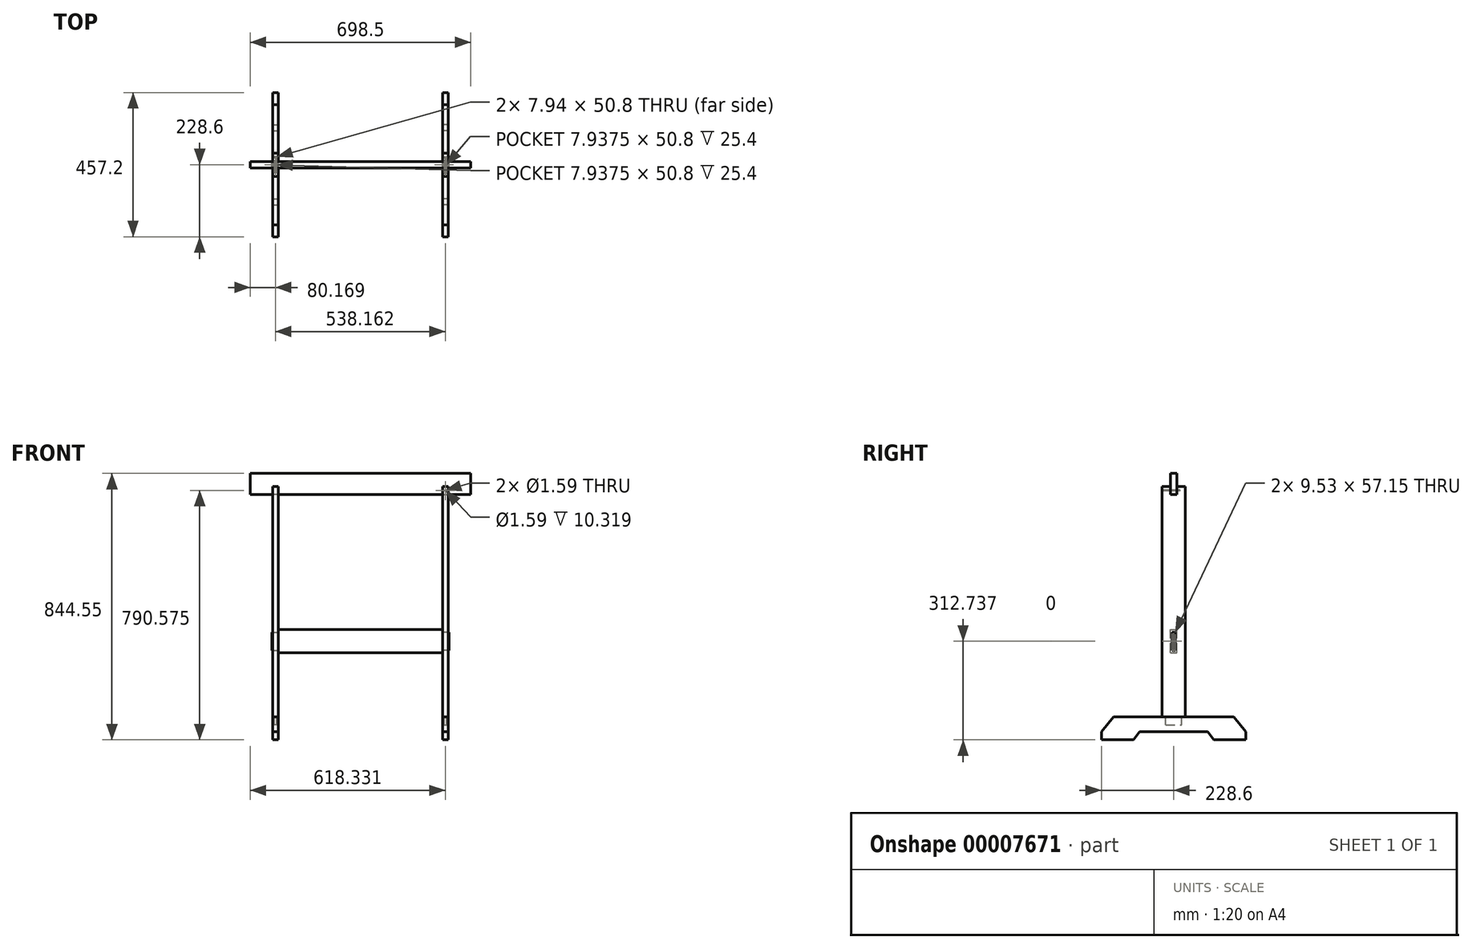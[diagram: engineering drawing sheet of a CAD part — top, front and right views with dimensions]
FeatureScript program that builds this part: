
annotation { "Feature Type Name" : "Feature", "Feature Type Description" : "" }
export const myFeature = defineFeature(function(context is Context, id is Id, definition is map)
    precondition{}
    {
        {
            var Q0;
            Q0=qCreatedBy(makeId("Right.planeOp"),FACE);
            var sketch = newSketch(context, id + "F0", { "sketchPlane" : qUnion([Q0])});
            skLineSegment(sketch, "E0.bottom", {"start": v(-36.51, 365.13) * mm, "end": v(36.51, 365.13) * mm});
            skLineSegment(sketch, "E0.top", {"start": v(-36.51, -365.13) * mm, "end": v(36.51, -365.13) * mm});
            skLineSegment(sketch, "E0.left", {"start": v(-36.51, 365.12) * mm, "end": v(-36.51, -365.13) * mm});
            skLineSegment(sketch, "E0.right", {"start": v(36.51, 365.13) * mm, "end": v(36.51, -365.13) * mm});
            skPoint(sketch, "E1", {"position": v(-36.51, 0) * mm});
            skPoint(sketch, "E2", {"position": v(0, 365.13) * mm});
            skPoint(sketch, "E3", {"position": v(0, -365.13) * mm});
            skSolve(sketch);
        }
        {
            var Q0;
            Q0=makeQuery(id+"F0.imprint","IMPRINT",FACE,{"disambiguationData":[TD([[makeQuery(id+"F0.imprint","IMPRINT",EDGE,{"derivedFrom":sQuery(id+"F0.wireOp",EDGE,"E0.bottom")}),-1.0]])]});
            extrude(context, id + "F1", {"entities" : qUnion([Q0]), "depth" : 17.46 * mm});
        }
        {
            var Q0;
            Q0=makeQuery(id+"F1.opExtrude","SWEPT_FACE",FACE,{"disambiguationData":[OSD([sQuery(id+"F0.wireOp",EDGE,"E0.top")])]});
            var sketch = newSketch(context, id + "F2", { "sketchPlane" : qUnion([Q0])});
            skLineSegment(sketch, "E4.bottom", {"start": v(4.76, 25.4) * mm, "end": v(12.7, 25.4) * mm});
            skLineSegment(sketch, "E4.top", {"start": v(4.76, -25.4) * mm, "end": v(12.7, -25.4) * mm});
            skLineSegment(sketch, "E4.left", {"start": v(4.76, 25.4) * mm, "end": v(4.76, -25.4) * mm});
            skLineSegment(sketch, "E4.right", {"start": v(12.7, 25.4) * mm, "end": v(12.7, -25.4) * mm});
            skPoint(sketch, "E5", {"position": v(4.76, 0) * mm});
            skPoint(sketch, "E6", {"position": v(8.73, 25.4) * mm});
            skLineSegment(sketch, "E7", {"start": v(0, 36.51) * mm, "end": v(17.46, 36.51) * mm, "construction": true});
            skPoint(sketch, "E8", {"position": v(8.73, 36.51) * mm});
            skSolve(sketch);
        }
        {
            var Q0;
            Q0=makeQuery(id+"F2.imprint","IMPRINT",FACE,{"disambiguationData":[TD([[makeQuery(id+"F2.imprint","IMPRINT",EDGE,{"derivedFrom":sQuery(id+"F2.wireOp",EDGE,"E4.bottom")}),-1.0]])]});
            extrude(context, id + "F3", {"entities" : qUnion([Q0]), "operationType" : NewBodyOperationType.ADD, "depth" : 25.4 * mm});
        }
        {
            var Q0;
            Q0=makeQuery(id+"FvcOJnYdktQ8z6b_1.boolean.opBoolean","MERGE",FACE,{"derivedFrom":[makeQuery(id+"F1.opExtrude","CAP_FACE",FACE,{"disambiguationData":[OSD([sQuery(id+"F0.wireOp",EDGE,"E0.bottom"),sQuery(id+"F0.wireOp",EDGE,"E0.top"),sQuery(id+"F0.wireOp",EDGE,"E0.left"),sQuery(id+"F0.wireOp",EDGE,"E0.right")])],"isStart":false}),makeQuery(id+"FvcOJnYdktQ8z6b_1.opExtrude","CAP_FACE",FACE,{"disambiguationData":[OSD([sQuery(id+"FRvuE240jbc6a3C_1.wireOp",EDGE,"65dea670-6dc7-43e9-8bfd-74e16df26cca.bottom"),sQuery(id+"FRvuE240jbc6a3C_1.wireOp",EDGE,"65dea670-6dc7-43e9-8bfd-74e16df26cca.top"),sQuery(id+"FRvuE240jbc6a3C_1.wireOp",EDGE,"65dea670-6dc7-43e9-8bfd-74e16df26cca.left"),sQuery(id+"FRvuE240jbc6a3C_1.wireOp",EDGE,"65dea670-6dc7-43e9-8bfd-74e16df26cca.right")])],"isStart":false})]});
            var sketch = newSketch(context, id + "F4", { "sketchPlane" : qUnion([Q0])});
            skLineSegment(sketch, "E9.bottom", {"start": v(-10.32, 365.13) * mm, "end": v(10.32, 365.13) * mm});
            skLineSegment(sketch, "E9.top", {"start": v(-10.32, 339.73) * mm, "end": v(10.32, 339.73) * mm});
            skLineSegment(sketch, "E9.left", {"start": v(-10.32, 365.13) * mm, "end": v(-10.32, 339.73) * mm});
            skLineSegment(sketch, "E9.right", {"start": v(10.32, 365.13) * mm, "end": v(10.32, 339.73) * mm});
            skPoint(sketch, "E10", {"position": v(0, 365.13) * mm});
            skSolve(sketch);
        }
        {
            var Q0;
            Q0=makeQuery(id+"F4.imprint","IMPRINT",FACE,{"disambiguationData":[TD([[makeQuery(id+"F4.imprint","IMPRINT",EDGE,{"derivedFrom":sQuery(id+"F4.wireOp",EDGE,"E9.bottom")}),-1.0]])]});
            var Q1;
            Q1=makeQuery(id+"FvcOJnYdktQ8z6b_1.boolean.opBoolean","MERGE",FACE,{"derivedFrom":[makeQuery(id+"F1.opExtrude","CAP_FACE",FACE,{"disambiguationData":[OSD([sQuery(id+"F0.wireOp",EDGE,"E0.bottom"),sQuery(id+"F0.wireOp",EDGE,"E0.top"),sQuery(id+"F0.wireOp",EDGE,"E0.left"),sQuery(id+"F0.wireOp",EDGE,"E0.right")])],"isStart":true}),makeQuery(id+"FvcOJnYdktQ8z6b_1.opExtrude","CAP_FACE",FACE,{"disambiguationData":[OSD([sQuery(id+"FRvuE240jbc6a3C_1.wireOp",EDGE,"65dea670-6dc7-43e9-8bfd-74e16df26cca.bottom"),sQuery(id+"FRvuE240jbc6a3C_1.wireOp",EDGE,"65dea670-6dc7-43e9-8bfd-74e16df26cca.top"),sQuery(id+"FRvuE240jbc6a3C_1.wireOp",EDGE,"65dea670-6dc7-43e9-8bfd-74e16df26cca.left"),sQuery(id+"FRvuE240jbc6a3C_1.wireOp",EDGE,"65dea670-6dc7-43e9-8bfd-74e16df26cca.right")])],"isStart":true})]});
            extrude(context, id + "F5", {"entities" : qUnion([Q0]), "operationType" : NewBodyOperationType.REMOVE, "endBound" : BoundingType.UP_TO_SURFACE, "oppositeDirection" : true, "endBoundEntityFace" : qUnion([Q1]), "depth" : 25.4 * mm});
        }
        {
            var Q0;
            Q0=qCreatedBy(makeId("Right.planeOp"),FACE);
            var sketch = newSketch(context, id + "F6", { "sketchPlane" : qUnion([Q0])});
            skLineSegment(sketch, "E11.bottom", {"start": v(-190.5, -365.13) * mm, "end": v(190.5, -365.13) * mm});
            skLineSegment(sketch, "E11.top", {"start": v(-228.6, -438.15) * mm, "end": v(-127, -438.15) * mm});
            skLineSegment(sketch, "E11.left", {"start": v(-228.6, -412.75) * mm, "end": v(-228.6, -438.15) * mm});
            skLineSegment(sketch, "E11.right", {"start": v(228.6, -412.75) * mm, "end": v(228.6, -438.15) * mm});
            skPoint(sketch, "E12", {"position": v(0, -438.15) * mm});
            skLineSegment(sketch, "E13", {"start": v(-228.6, -438.15) * mm, "end": v(-228.6, -412.75) * mm, "construction": true});
            skLineSegment(sketch, "E14", {"start": v(-228.6, -412.75) * mm, "end": v(-190.5, -365.13) * mm});
            skLineSegment(sketch, "E15", {"start": v(-190.5, -365.13) * mm, "end": v(-228.6, -365.13) * mm, "construction": true});
            skLineSegment(sketch, "E16", {"start": v(0, -438.15) * mm, "end": v(0, -365.13) * mm, "construction": true});
            skLineSegment(sketch, "E17", {"start": v(0, -438.15) * mm, "end": v(-127, -438.15) * mm, "construction": true});
            skLineSegment(sketch, "E18", {"start": v(-127, -438.15) * mm, "end": v(-108.04, -412.75) * mm});
            skLineSegment(sketch, "E19", {"start": v(-108.04, -412.75) * mm, "end": v(108.04, -412.75) * mm});
            skLineSegment(sketch, "E20.0.MirrorCS", {"start": v(228.6, -412.75) * mm, "end": v(190.5, -365.13) * mm});
            skLineSegment(sketch, "E21.0.MirrorCS", {"start": v(127, -438.15) * mm, "end": v(108.04, -412.75) * mm});
            skLineSegment(sketch, "E22.trimOffspring", {"start": v(127, -438.15) * mm, "end": v(228.6, -438.15) * mm});
            skLineSegment(sketch, "E23", {"start": v(0, -498.51) * mm, "end": v(-228.6, -498.51) * mm});
            skSolve(sketch);
        }
        {
            var Q0;
            Q0=makeQuery(id+"F6.imprint","IMPRINT",FACE,{"disambiguationData":[TD([[makeQuery(id+"F6.imprint","IMPRINT",EDGE,{"derivedFrom":sQuery(id+"F6.wireOp",EDGE,"E11.bottom")}),-1.0]])]});
            var Q1;
            Q1=makeQuery(id+"FvcOJnYdktQ8z6b_1.boolean.opBoolean","MERGE",FACE,{"derivedFrom":[makeQuery(id+"F1.opExtrude","CAP_FACE",FACE,{"disambiguationData":[OSD([sQuery(id+"F0.wireOp",EDGE,"E0.bottom"),sQuery(id+"F0.wireOp",EDGE,"E0.top"),sQuery(id+"F0.wireOp",EDGE,"E0.left"),sQuery(id+"F0.wireOp",EDGE,"E0.right")])],"isStart":false}),makeQuery(id+"FvcOJnYdktQ8z6b_1.opExtrude","CAP_FACE",FACE,{"disambiguationData":[OSD([sQuery(id+"FRvuE240jbc6a3C_1.wireOp",EDGE,"65dea670-6dc7-43e9-8bfd-74e16df26cca.bottom"),sQuery(id+"FRvuE240jbc6a3C_1.wireOp",EDGE,"65dea670-6dc7-43e9-8bfd-74e16df26cca.top"),sQuery(id+"FRvuE240jbc6a3C_1.wireOp",EDGE,"65dea670-6dc7-43e9-8bfd-74e16df26cca.left"),sQuery(id+"FRvuE240jbc6a3C_1.wireOp",EDGE,"65dea670-6dc7-43e9-8bfd-74e16df26cca.right")])],"isStart":false})]});
            extrude(context, id + "F7", {"entities" : qUnion([Q0]), "endBound" : BoundingType.UP_TO_SURFACE, "endBoundEntityFace" : qUnion([Q1]), "depth" : 25.4 * mm});
        }
        {
            var Q0;
            Q0=makeQuery(id+"F1.opExtrude","SWEPT_BODY",BODY,{"disambiguationData":[OSD([sQuery(id+"F0.wireOp",EDGE,"E0.bottom"),sQuery(id+"F0.wireOp",EDGE,"E0.top"),sQuery(id+"F0.wireOp",EDGE,"E0.left"),sQuery(id+"F0.wireOp",EDGE,"E0.right")])]});
            var Q1;
            Q1=makeQuery(id+"F7.opExtrude","SWEPT_BODY",BODY,{"disambiguationData":[OSD([sQuery(id+"F6.wireOp",EDGE,"E11.bottom"),sQuery(id+"F6.wireOp",EDGE,"E11.top"),sQuery(id+"F6.wireOp",EDGE,"E11.left"),sQuery(id+"F6.wireOp",EDGE,"E11.right"),sQuery(id+"F6.wireOp",EDGE,"E14"),sQuery(id+"F6.wireOp",EDGE,"E18"),sQuery(id+"F6.wireOp",EDGE,"E19"),sQuery(id+"F6.wireOp",EDGE,"E20.0.MirrorCS"),sQuery(id+"F6.wireOp",EDGE,"E21.0.MirrorCS"),sQuery(id+"F6.wireOp",EDGE,"E22.trimOffspring")])]});
            booleanBodies(context, id + "F8", {"operationType" : BooleanOperationType.SUBTRACTION, "tools" : qUnion([Q0]), "targets" : qUnion([Q1]), "keepTools" : true});
        }
        {
            var Q0;
            Q0=qCreatedBy(makeId("Front.planeOp"),FACE);
            var sketch = newSketch(context, id + "F9", { "sketchPlane" : qUnion([Q0])});
            skLineSegment(sketch, "E24", {"start": v(0, -365.13) * mm, "end": v(0, -161.93) * mm});
            skLineSegment(sketch, "E25.bottom", {"start": v(0, -161.93) * mm, "end": v(-520.7, -161.93) * mm});
            skLineSegment(sketch, "E25.top", {"start": v(0, -88.9) * mm, "end": v(-520.7, -88.9) * mm});
            skLineSegment(sketch, "E25.left", {"start": v(0, -161.93) * mm, "end": v(0, -88.9) * mm});
            skLineSegment(sketch, "E25.right", {"start": v(-520.7, -161.93) * mm, "end": v(-520.7, -88.9) * mm});
            skPoint(sketch, "E26", {"position": v(-260.35, -88.9) * mm});
            skSolve(sketch);
        }
        {
            var Q0;
            Q0=makeQuery(id+"F9.imprint","IMPRINT",FACE,{"disambiguationData":[TD([[makeQuery(id+"F9.imprint","IMPRINT",EDGE,{"derivedFrom":sQuery(id+"F9.wireOp",EDGE,"E25.bottom")}),-1.0]])]});
            extrude(context, id + "F10", {"entities" : qUnion([Q0]), "endBound" : BoundingType.SYMMETRIC, "depth" : 20.64 * mm});
        }
        {
            var Q0;
            Q0=makeQuery(id+"F10.opExtrude","SWEPT_FACE",FACE,{"disambiguationData":[OSD([sQuery(id+"F9.wireOp",EDGE,"E25.right")])]});
            var sketch = newSketch(context, id + "F11", { "sketchPlane" : qUnion([Q0])});
            skLineSegment(sketch, "E27.rect.bottom", {"start": v(4.76, -96.84) * mm, "end": v(-4.76, -96.84) * mm});
            skLineSegment(sketch, "E27.rect.top", {"start": v(4.76, -153.99) * mm, "end": v(-4.76, -153.99) * mm});
            skLineSegment(sketch, "E27.rect.left", {"start": v(4.76, -96.84) * mm, "end": v(4.76, -153.99) * mm});
            skLineSegment(sketch, "E27.rect.right", {"start": v(-4.76, -96.84) * mm, "end": v(-4.76, -153.99) * mm});
            skPoint(sketch, "E27.rect.middle", {"position": v(0, -125.41) * mm});
            skPoint(sketch, "E28", {"position": v(-10.32, -125.41) * mm});
            skSolve(sketch);
        }
        {
            var Q0;
            Q0=makeQuery(id+"F11.imprint","IMPRINT",FACE,{"disambiguationData":[TD([[makeQuery(id+"F11.imprint","IMPRINT",EDGE,{"derivedFrom":sQuery(id+"F11.wireOp",EDGE,"E27.rect.bottom")}),1.0]])]});
            extrude(context, id + "F12", {"entities" : qUnion([Q0]), "depth" : 20.64 * mm});
        }
        {
            var Q0;
            Q0=makeQuery(id+"F10.opExtrude","SWEPT_FACE",FACE,{"disambiguationData":[OSD([sQuery(id+"F9.wireOp",EDGE,"E25.top")])]});
            var sketch = newSketch(context, id + "F13", { "sketchPlane" : qUnion([Q0])});
            skLineSegment(sketch, "E29", {"start": v(-260.35, 10.32) * mm, "end": v(-260.35, -10.32) * mm});
            skSolve(sketch);
        }
        {
            var Q0;
            Q0=sQuery(id+"F13.wireOp",EDGE,"E29");
            cPlane(context, id + "F14", {"entities" : qUnion([Q0]), "cplaneType" : CPlaneType.LINE_ANGLE, "offset" : 152.4 * mm, "angle" : 90 * degree, "width" : 152.4 * mm, "height" : 152.4 * mm});
        }
        {
            var Q0;
            Q0=makeQuery(id+"F12.opExtrude","SWEPT_BODY",BODY,{"disambiguationData":[OSD([sQuery(id+"F11.wireOp",EDGE,"E27.rect.bottom"),sQuery(id+"F11.wireOp",EDGE,"E27.rect.top"),sQuery(id+"F11.wireOp",EDGE,"E27.rect.left"),sQuery(id+"F11.wireOp",EDGE,"E27.rect.right")])]});
            var Q1;
            Q1=makeQuery(id+"F1.opExtrude","SWEPT_BODY",BODY,{"disambiguationData":[OSD([sQuery(id+"F0.wireOp",EDGE,"E0.bottom"),sQuery(id+"F0.wireOp",EDGE,"E0.top"),sQuery(id+"F0.wireOp",EDGE,"E0.left"),sQuery(id+"F0.wireOp",EDGE,"E0.right")])]});
            var Q2;
            Q2=makeQuery(id+"F7.opExtrude","SWEPT_BODY",BODY,{"disambiguationData":[OSD([sQuery(id+"F6.wireOp",EDGE,"E11.bottom"),sQuery(id+"F6.wireOp",EDGE,"E11.top"),sQuery(id+"F6.wireOp",EDGE,"E11.left"),sQuery(id+"F6.wireOp",EDGE,"E11.right"),sQuery(id+"F6.wireOp",EDGE,"E14"),sQuery(id+"F6.wireOp",EDGE,"E18"),sQuery(id+"F6.wireOp",EDGE,"E19"),sQuery(id+"F6.wireOp",EDGE,"E20.0.MirrorCS"),sQuery(id+"F6.wireOp",EDGE,"E21.0.MirrorCS"),sQuery(id+"F6.wireOp",EDGE,"E22.trimOffspring")])]});
            var Q3;
            Q3=qCreatedBy(id+"F14.planeOp",FACE);
            mirror(context, id + "F15", {"entities" : qUnion([Q0, Q1, Q2]), "mirrorPlane" : qUnion([Q3])});
        }
        {
            var Q0;
            Q0=makeQuery(id+"F15.opPattern","COPY",BODY,{"derivedFrom":makeQuery(id+"F12.opExtrude","SWEPT_BODY",BODY,{"disambiguationData":[OSD([sQuery(id+"F11.wireOp",EDGE,"E27.rect.bottom"),sQuery(id+"F11.wireOp",EDGE,"E27.rect.top"),sQuery(id+"F11.wireOp",EDGE,"E27.rect.left"),sQuery(id+"F11.wireOp",EDGE,"E27.rect.right")])]}),"instanceName":"1"});
            var Q1;
            Q1=makeQuery(id+"F12.opExtrude","SWEPT_BODY",BODY,{"disambiguationData":[OSD([sQuery(id+"F11.wireOp",EDGE,"E27.rect.bottom"),sQuery(id+"F11.wireOp",EDGE,"E27.rect.top"),sQuery(id+"F11.wireOp",EDGE,"E27.rect.left"),sQuery(id+"F11.wireOp",EDGE,"E27.rect.right")])]});
            var Q2;
            Q2=makeQuery(id+"F15.opPattern","COPY",BODY,{"derivedFrom":makeQuery(id+"F1.opExtrude","SWEPT_BODY",BODY,{"disambiguationData":[OSD([sQuery(id+"F0.wireOp",EDGE,"E0.bottom"),sQuery(id+"F0.wireOp",EDGE,"E0.top"),sQuery(id+"F0.wireOp",EDGE,"E0.left"),sQuery(id+"F0.wireOp",EDGE,"E0.right")])]}),"instanceName":"1"});
            var Q3;
            Q3=makeQuery(id+"F1.opExtrude","SWEPT_BODY",BODY,{"disambiguationData":[OSD([sQuery(id+"F0.wireOp",EDGE,"E0.bottom"),sQuery(id+"F0.wireOp",EDGE,"E0.top"),sQuery(id+"F0.wireOp",EDGE,"E0.left"),sQuery(id+"F0.wireOp",EDGE,"E0.right")])]});
            booleanBodies(context, id + "F16", {"operationType" : BooleanOperationType.SUBTRACTION, "tools" : qUnion([Q0, Q1]), "targets" : qUnion([Q2, Q3]), "keepTools" : true});
        }
        {
            var Q0;
            Q0=qCreatedBy(makeId("Front.planeOp"),FACE);
            var sketch = newSketch(context, id + "F17", { "sketchPlane" : qUnion([Q0])});
            skLineSegment(sketch, "E30.bottom", {"start": v(88.9, 406.4) * mm, "end": v(-609.6, 406.4) * mm});
            skLineSegment(sketch, "E30.top", {"start": v(88.9, 339.73) * mm, "end": v(-609.6, 339.73) * mm});
            skLineSegment(sketch, "E30.left", {"start": v(88.9, 406.4) * mm, "end": v(88.9, 339.73) * mm});
            skLineSegment(sketch, "E30.right", {"start": v(-609.6, 406.4) * mm, "end": v(-609.6, 339.73) * mm});
            skPoint(sketch, "E31", {"position": v(-260.35, 339.73) * mm});
            skSolve(sketch);
        }
        {
            var Q0;
            Q0=makeQuery(id+"F17.imprint","IMPRINT",FACE,{"disambiguationData":[TD([[makeQuery(id+"F17.imprint","IMPRINT",EDGE,{"derivedFrom":sQuery(id+"F17.wireOp",EDGE,"E30.bottom")}),1.0]])]});
            extrude(context, id + "F18", {"entities" : qUnion([Q0]), "endBound" : BoundingType.SYMMETRIC, "depth" : 20.64 * mm});
        }
        {
            var Q0;
            Q0=makeQuery(id+"F1.opExtrude","SWEPT_FACE",FACE,{"disambiguationData":[OSD([sQuery(id+"F0.wireOp",EDGE,"E0.left")])]});
            var sketch = newSketch(context, id + "F19", { "sketchPlane" : qUnion([Q0])});
            skCircle(sketch, "E32", {"center": v(8.73, 352.43) * mm, "radius": 0.8 * mm});
            skLineSegment(sketch, "E33", {"start": v(8.73, 365.12) * mm, "end": v(8.73, 352.43) * mm, "construction": true});
            skSolve(sketch);
        }
        {
            var Q0;
            Q0=makeQuery(id+"F19.imprint","IMPRINT",FACE,{"disambiguationData":[TD([[makeQuery(id+"F19.imprint","IMPRINT",EDGE,{"derivedFrom":sQuery(id+"F19.wireOp",EDGE,"E32")}),1.0]])]});
            extrude(context, id + "F20", {"entities" : qUnion([Q0]), "operationType" : NewBodyOperationType.REMOVE, "oppositeDirection" : true, "depth" : 57.15 * mm});
        }
    });
